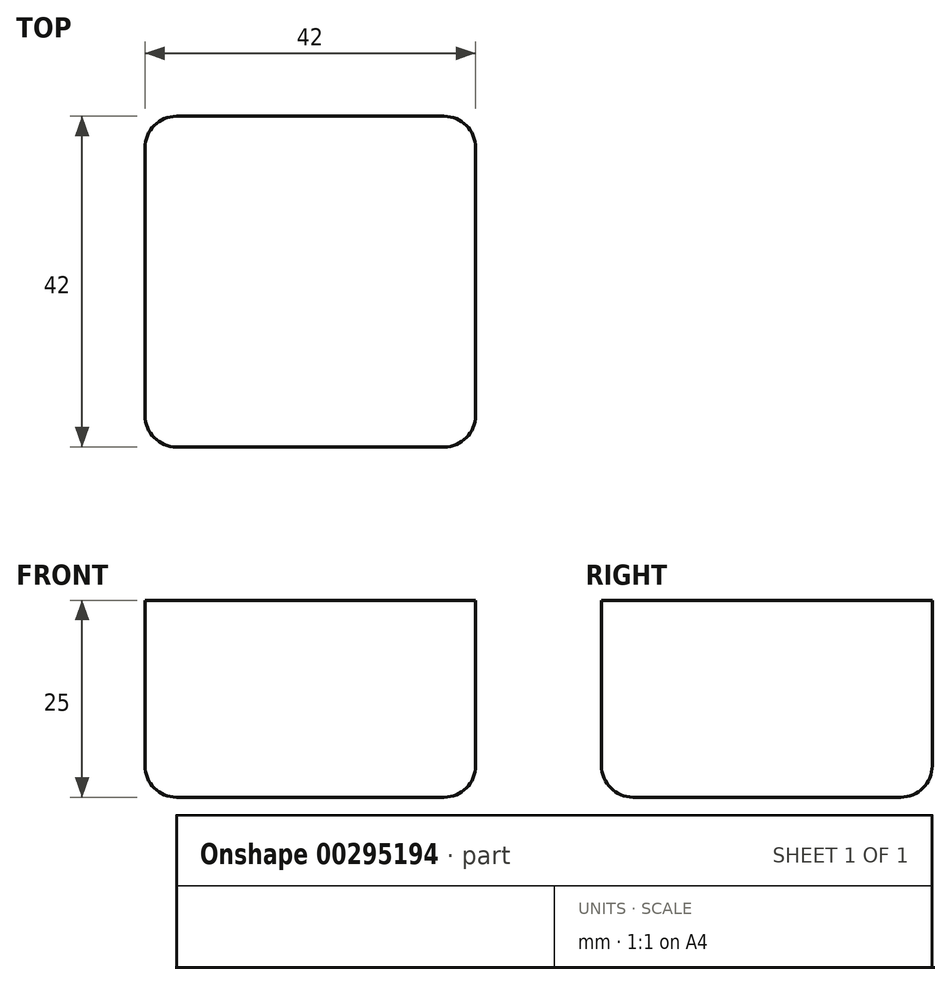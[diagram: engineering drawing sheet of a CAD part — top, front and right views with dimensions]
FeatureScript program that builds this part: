
annotation { "Feature Type Name" : "Feature", "Feature Type Description" : "" }
export const myFeature = defineFeature(function(context is Context, id is Id, definition is map)
    precondition{}
    {
        {
            var Q0;
            Q0=qCreatedBy(makeId("Top.planeOp"),FACE);
            var sketch = newSketch(context, id + "F0", { "sketchPlane" : qUnion([Q0])});
            skLineSegment(sketch, "E0.bottom", {"start": v(21, 21) * mm, "end": v(-21, 21) * mm});
            skLineSegment(sketch, "E0.top", {"start": v(21, -21) * mm, "end": v(-21, -21) * mm});
            skLineSegment(sketch, "E0.left", {"start": v(21, 21) * mm, "end": v(21, -21) * mm});
            skLineSegment(sketch, "E0.right", {"start": v(-21, 21) * mm, "end": v(-21, -21) * mm});
            skPoint(sketch, "E0.middle", {"position": v(0, 0) * mm});
            skSolve(sketch);
        }
        {
            var Q0;
            Q0=qSketchRegion(id+"F0",true);
            extrude(context, id + "F1", {"entities" : qUnion([Q0]), "depth" : 40 * mm});
        }
        {
            var Q0;
            Q0=makeQuery(id+"F1.opExtrude","SWEPT_FACE",FACE,{"disambiguationData":[OSD([sQuery(id+"F0.wireOp",EDGE,"E0.top")])]});
            var Q1;
            Q1=makeQuery(id+"F1.opExtrude","CAP_FACE",FACE,{"disambiguationData":[OSD([sQuery(id+"F0.wireOp",EDGE,"E0.bottom"),sQuery(id+"F0.wireOp",EDGE,"E0.top"),sQuery(id+"F0.wireOp",EDGE,"E0.left"),sQuery(id+"F0.wireOp",EDGE,"E0.right")])],"isStart":false});
            var Q2;
            Q2=makeQuery(id+"F1.opExtrude","SWEPT_FACE",FACE,{"disambiguationData":[OSD([sQuery(id+"F0.wireOp",EDGE,"E0.left")])]});
            var Q3;
            Q3=makeQuery(id+"F1.opExtrude","SWEPT_FACE",FACE,{"disambiguationData":[OSD([sQuery(id+"F0.wireOp",EDGE,"E0.bottom")])]});
            var Q4;
            Q4=makeQuery(id+"F1.opExtrude","SWEPT_FACE",FACE,{"disambiguationData":[OSD([sQuery(id+"F0.wireOp",EDGE,"E0.right")])]});
            fillet(context, id + "F2", {"entities" : qUnion([Q0, Q1, Q2, Q3, Q4]), "radius" : 4 * mm, "tangentPropagation" : true, "allowEdgeOverflow" : false});
        }
        {
            var Q0;
            Q0=makeQuery(id+"F1.opExtrude","CAP_FACE",FACE,{"disambiguationData":[OSD([sQuery(id+"F0.wireOp",EDGE,"E0.bottom"),sQuery(id+"F0.wireOp",EDGE,"E0.top"),sQuery(id+"F0.wireOp",EDGE,"E0.left"),sQuery(id+"F0.wireOp",EDGE,"E0.right")])],"isStart":false});
            var sketch = newSketch(context, id + "F3", { "sketchPlane" : qUnion([Q0])});
            skLineSegment(sketch, "E1.bottom", {"start": v(25.7, 31.06) * mm, "end": v(-25.7, 31.06) * mm});
            skLineSegment(sketch, "E1.top", {"start": v(25.7, -31.06) * mm, "end": v(-25.7, -31.06) * mm});
            skLineSegment(sketch, "E1.left", {"start": v(25.7, 31.06) * mm, "end": v(25.7, -31.06) * mm});
            skLineSegment(sketch, "E1.right", {"start": v(-25.7, 31.06) * mm, "end": v(-25.7, -31.06) * mm});
            skPoint(sketch, "E1.middle", {"position": v(0, 0) * mm});
            skSolve(sketch);
        }
        {
            var Q0;
            Q0=makeQuery(id+"F3.imprint","IMPRINT",FACE,{"disambiguationData":[TD([[makeQuery(id+"F3.imprint","IMPRINT",EDGE,{"derivedFrom":sQuery(id+"F3.wireOp",EDGE,"E1.bottom")}),1.0]])]});
            var Q1;
            {var subQ0=sQuery(id+"F0.wireOp",EDGE,"E0.right");var subQ1=sQuery(id+"F0.wireOp",EDGE,"E0.left");var subQ2=sQuery(id+"F0.wireOp",EDGE,"E0.top");var subQ3=sQuery(id+"F0.wireOp",EDGE,"E0.bottom");var subQ4=makeQuery(id+"F1.opExtrude","CAP_FACE",FACE,{"disambiguationData":[OSD([subQ3,subQ2,subQ1,subQ0])],"isStart":false});Q1=makeQuery(id+"F3.imprint","IMPRINT",FACE,{"disambiguationData":[TD([[makeQuery(id+"F3.imprint","IMPRINT",EDGE,{"derivedFrom":makeQuery(id+"F2.opFillet","BLEND_EDGE",EDGE,{"blendedFrom":[makeQuery(id+"F1.opExtrude","CAP_EDGE",EDGE,{"disambiguationData":[OSD([subQ3])],"isStart":false}),subQ4],"blendedInto":[subQ4]})}),1.0]])]});}
            extrude(context, id + "F4", {"entities" : qUnion([Q0, Q1]), "operationType" : NewBodyOperationType.REMOVE, "oppositeDirection" : true, "depth" : 15 * mm});
        }
    });
